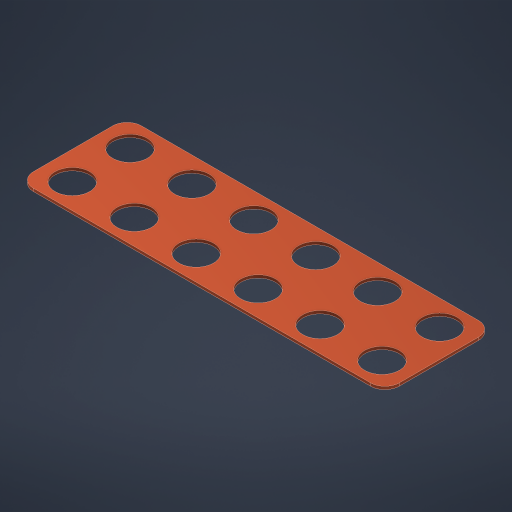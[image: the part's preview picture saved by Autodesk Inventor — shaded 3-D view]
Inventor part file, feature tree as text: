
AUTODESK INVENTOR PART (.ipt)
format: ipt  version: 2024.3 (Build 283343010, 343A)  size: 259,584 bytes
history: native  units: mm
features: sketch x2, extrude x1, fillet x1, projected_geometry x1
ambient origin geometry x8: Origin, YZ Plane, XZ Plane, XY Plane, X Axis, Y Axis, Z Axis, Center Point
bodies: Volumenkörper1 (feature_tree)
feature tree (5):
  extrude  "Extrusion1"  Depth=37.5mm
  fillet  "Rundung1"  Radius=21.5mm
  sketch  "Skizze2"  dims[d14=1.0mm d15=0.0mm d16=5.0mm d17=43.0mm d18=21.5mm d19=12.0mm d20=10.0mm d21=60.0mm d23=21.5mm d24=20.0mm d26=20.0mm d29=10.75mm]
  sketch  "Skizze1"  dims[d0=127.0mm d1=37.5mm d9=21.5mm]
  projected_geometry  "Projizierte Kontur1"
